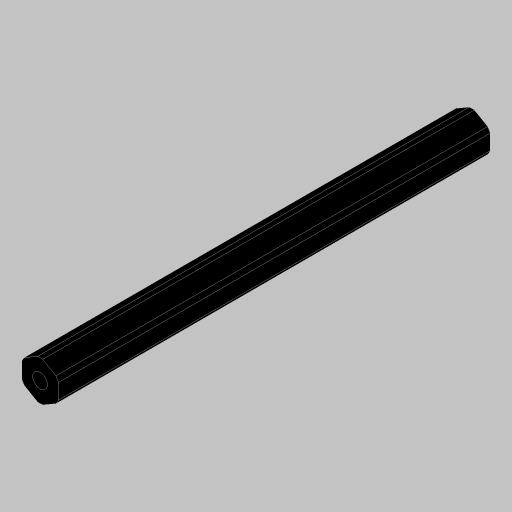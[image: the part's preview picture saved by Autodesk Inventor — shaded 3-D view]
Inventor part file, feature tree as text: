
AUTODESK INVENTOR PART (.ipt)
format: ipt  version: 2023.5 (Build 275446000, 446)  size: 118,784 bytes
history: native  units: in
note: dims shown in document units (in); Inventor stores cm internally (conversion verified against a paired STEP export)
features: extrude x2, projected_geometry x2, hole x1
ambient origin geometry x8: Origin, YZ Plane, XZ Plane, XY Plane, X Axis, Y Axis, Z Axis, Center Point
bodies: Solid1 (feature_tree)
feature tree (5):
  extrude  "Extrusion1"  TaperAngle=0.0deg  [1 undecoded]
  hole  "Hole1"  [1 undecoded]
  extrude  "Extrusion3"  TaperAngle=0.0deg  [1 undecoded]
  projected_geometry  "Project Cut Edges1"
  projected_geometry  "Project Cut Edges2"
note: 3 required parameter values undecoded (feature->parameter linkage not recoverable at this tier; creation-order binding heuristic only, values carry confidence <= 0.55)
